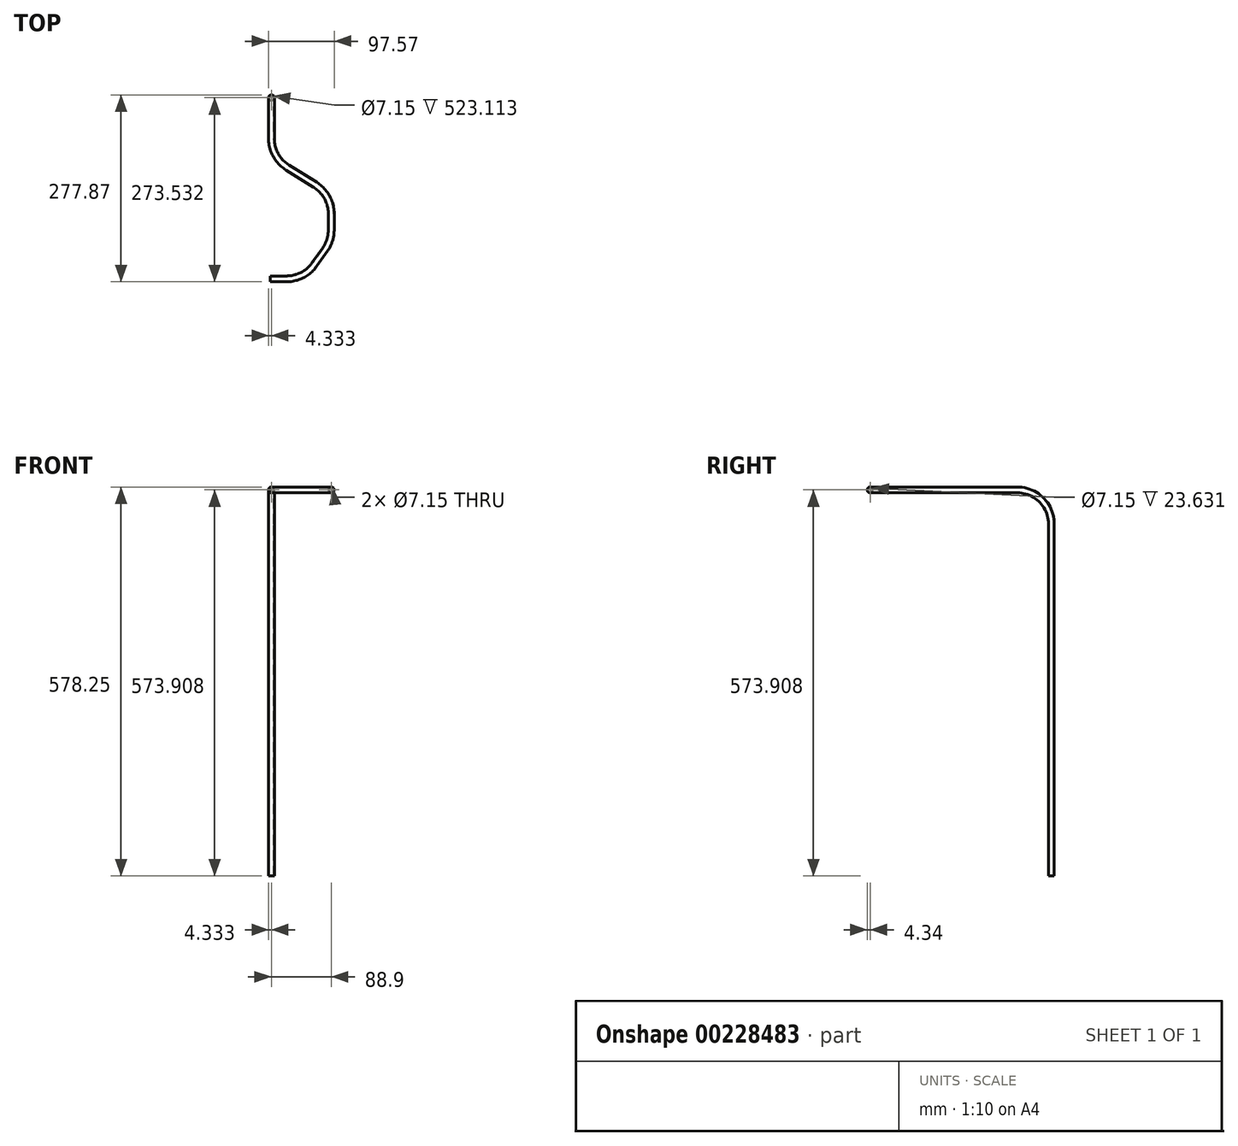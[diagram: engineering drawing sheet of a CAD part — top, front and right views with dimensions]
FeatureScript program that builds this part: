
annotation { "Feature Type Name" : "Feature", "Feature Type Description" : "" }
export const myFeature = defineFeature(function(context is Context, id is Id, definition is map)
    precondition{}
    {
        {
            var Q0;
            Q0=qCreatedBy(makeId("Top.planeOp"),FACE);
            var sketch = newSketch(context, id + "F0", { "sketchPlane" : qUnion([Q0])});
            skLineSegment(sketch, "E0", {"start": v(0, 0) * mm, "end": v(80.3, 0) * mm});
            skLineSegment(sketch, "E1", {"start": v(80.3, 0) * mm, "end": v(80.3, -94.46) * mm});
            skLineSegment(sketch, "E2", {"start": v(80.3, -94.46) * mm, "end": v(54.9, -94.46) * mm});
            skLineSegment(sketch, "E3", {"start": v(0, 0) * mm, "end": v(1.24, 0) * mm});
            skLineSegment(sketch, "E4", {"start": v(1.24, 0) * mm, "end": v(1.24, -0.8) * mm});
            skLineSegment(sketch, "E5", {"start": v(1.24, -0.8) * mm, "end": v(26.64, -0.8) * mm});
            skLineSegment(sketch, "E6", {"start": v(0, 0) * mm, "end": v(82.11, 0) * mm});
            skLineSegment(sketch, "E7.MirrorCS", {"start": v(82.11, 0) * mm, "end": v(82.11, 174.73) * mm});
            skLineSegment(sketch, "E8.MirrorCS", {"start": v(82.11, 174.73) * mm, "end": v(56.71, 174.73) * mm});
            skPoint(sketch, "E9.end.orphan", {"position": v(56.71, -174.73) * mm});
            skPoint(sketch, "E10.end.orphan", {"position": v(82.11, -174.73) * mm});
            skSolve(sketch);
        }
        {
            var Q0;
            Q0=sQuery(id+"F0.wireOp",EDGE,"E5");
            cPlane(context, id + "F1", {"entities" : qUnion([Q0]), "cplaneType" : CPlaneType.LINE_ANGLE, "offset" : 25.4 * mm, "angle" : 0 * degree, "width" : 152.4 * mm, "height" : 152.4 * mm});
        }
        {
            var Q0;
            Q0=qCreatedBy(id+"F1.planeOp",FACE);
            var sketch = newSketch(context, id + "F2", { "sketchPlane" : qUnion([Q0])});
            skLineSegment(sketch, "E11", {"start": v(-26.64, 0) * mm, "end": v(-26.64, 1312.2) * mm});
            skLineSegment(sketch, "E12", {"start": v(-26.64, 1312.2) * mm, "end": v(-1.24, 1312.2) * mm});
            skSolve(sketch);
        }
        {
            var Q0;
            Q0=sQuery(id+"F0.wireOp",EDGE,"E8.MirrorCS");
            cPlane(context, id + "F3", {"entities" : qUnion([Q0]), "cplaneType" : CPlaneType.LINE_ANGLE, "offset" : 25.4 * mm, "angle" : 0 * degree, "width" : 152.4 * mm, "height" : 152.4 * mm});
        }
        {
            var Q0;
            Q0=qCreatedBy(id+"F3.planeOp",FACE);
            var sketch = newSketch(context, id + "F4", { "sketchPlane" : qUnion([Q0])});
            skLineSegment(sketch, "E13", {"start": v(82.11, 0) * mm, "end": v(82.11, 801.7) * mm});
            skLineSegment(sketch, "E14", {"start": v(82.11, 801.7) * mm, "end": v(56.71, 801.7) * mm});
            skSolve(sketch);
        }
        {
            var Q0;
            Q0=sQuery(id+"F0.wireOp",EDGE,"E2");
            cPlane(context, id + "F5", {"entities" : qUnion([Q0]), "cplaneType" : CPlaneType.LINE_ANGLE, "offset" : 25.4 * mm, "angle" : 0 * degree, "width" : 152.4 * mm, "height" : 152.4 * mm});
        }
        {
            var Q0;
            Q0=qCreatedBy(id+"F5.planeOp",FACE);
            var sketch = newSketch(context, id + "F6", { "sketchPlane" : qUnion([Q0])});
            skLineSegment(sketch, "E15", {"start": v(80.3, 0) * mm, "end": v(80.3, 1375.6) * mm});
            skLineSegment(sketch, "E16", {"start": v(80.3, 1375.6) * mm, "end": v(54.9, 1375.6) * mm});
            skSolve(sketch);
        }
        {
            var Q0;
            Q0=sQuery(id+"F6.wireOp",EDGE,"E16");
            cPlane(context, id + "F7", {"entities" : qUnion([Q0]), "cplaneType" : CPlaneType.LINE_ANGLE, "offset" : 25.4 * mm, "angle" : 90 * degree, "width" : 152.4 * mm, "height" : 152.4 * mm});
        }
        {
            var Q0;
            Q0=qCreatedBy(id+"F7.planeOp",FACE);
            var sketch = newSketch(context, id + "F8", { "sketchPlane" : qUnion([Q0])});
            skLineSegment(sketch, "E17", {"start": v(80.3, -94.46) * mm, "end": v(80.3, -69.06) * mm});
            skSolve(sketch);
        }
        {
            var Q0;
            Q0=sQuery(id+"F8.wireOp",EDGE,"E17");
            cPlane(context, id + "F9", {"entities" : qUnion([Q0]), "cplaneType" : CPlaneType.LINE_ANGLE, "offset" : 25.4 * mm, "angle" : 90 * degree, "width" : 152.4 * mm, "height" : 152.4 * mm});
        }
        {
            var Q0;
            Q0=qCreatedBy(id+"F9.planeOp",FACE);
            var sketch = newSketch(context, id + "F10", { "sketchPlane" : qUnion([Q0])});
            skCircle(sketch, "E18", {"center": v(-94.46, 1375.6) * mm, "radius": 4.34 * mm});
            skSolve(sketch);
        }
        {
            var Q0;
            Q0=sQuery(id+"F2.wireOp",EDGE,"E12");
            cPlane(context, id + "F11", {"entities" : qUnion([Q0]), "cplaneType" : CPlaneType.LINE_ANGLE, "offset" : 25.4 * mm, "angle" : 90 * degree, "width" : 152.4 * mm, "height" : 152.4 * mm});
        }
        {
            var Q0;
            Q0=sQuery(id+"F4.wireOp",EDGE,"E14");
            cPlane(context, id + "F12", {"entities" : qUnion([Q0]), "cplaneType" : CPlaneType.LINE_ANGLE, "offset" : 25.4 * mm, "angle" : 90 * degree, "width" : 152.4 * mm, "height" : 152.4 * mm});
        }
        {
            var Q0;
            Q0=qCreatedBy(id+"F12.planeOp",FACE);
            var sketch = newSketch(context, id + "F13", { "sketchPlane" : qUnion([Q0])});
            skCircle(sketch, "E19", {"center": v(82.11, 174.73) * mm, "radius": 4.34 * mm});
            skSolve(sketch);
        }
        {
            var Q0;
            Q0=sQuery(id+"F4.wireOp",EDGE,"E14");
            cPlane(context, id + "F14", {"entities" : qUnion([Q0]), "cplaneType" : CPlaneType.LINE_ANGLE, "offset" : 25.4 * mm, "angle" : 0 * degree, "width" : 152.4 * mm, "height" : 152.4 * mm});
        }
        {
            var Q0;
            Q0=qCreatedBy(id+"F14.planeOp",FACE);
            var sketch = newSketch(context, id + "F15", { "sketchPlane" : qUnion([Q0])});
            skLineSegment(sketch, "E20", {"start": v(82.11, 801.7) * mm, "end": v(82.11, 877.9) * mm});
            skSolve(sketch);
        }
        {
            var Q0;
            Q0=qCreatedBy(id+"F7.planeOp",FACE);
            var sketch = newSketch(context, id + "F16", { "sketchPlane" : qUnion([Q0])});
            skLineSegment(sketch, "E21", {"start": v(80.3, -94.46) * mm, "end": v(104.69, -94.46) * mm});
            skLineSegment(sketch, "E22", {"start": v(146.27, -72.85) * mm, "end": v(161.8, -50.73) * mm});
            skLineSegment(sketch, "E23", {"start": v(171.01, -21.54) * mm, "end": v(171.01, 2.27) * mm});
            skLineSegment(sketch, "E24", {"start": v(147.06, 45.39) * mm, "end": v(106.06, 70.92) * mm});
            skLineSegment(sketch, "E25", {"start": v(82.11, 114.04) * mm, "end": v(82.11, 174.73) * mm});
            skLineSegment(sketch, "E26", {"start": v(171.01, 30.48) * mm, "end": v(82.11, 30.48) * mm});
            skPoint(sketch, "E27.visualSharp", {"position": v(131.1, -94.46) * mm});
            skArc(sketch, "E27.filletArc", {"start": v(104.69, -94.46) * mm, "mid": v(128.12, -88.73) * mm, "end": v(146.27, -72.85) * mm});
            skPoint(sketch, "E28.visualSharp", {"position": v(171.01, -37.6) * mm});
            skArc(sketch, "E28.filletArc", {"start": v(161.8, -50.73) * mm, "mid": v(168.65, -36.85) * mm, "end": v(171.01, -21.54) * mm});
            skPoint(sketch, "E29.visualSharp", {"position": v(171.01, 30.48) * mm});
            skArc(sketch, "E29.filletArc", {"start": v(171.01, 2.27) * mm, "mid": v(164.62, 26.93) * mm, "end": v(147.06, 45.39) * mm});
            skPoint(sketch, "E30.visualSharp", {"position": v(82.11, 85.83) * mm});
            skArc(sketch, "E30.filletArc", {"start": v(82.11, 114.04) * mm, "mid": v(88.5, 89.38) * mm, "end": v(106.06, 70.92) * mm});
            skSolve(sketch);
        }
        {
            var Q0;
            Q0=sQuery(id+"F15.wireOp",VERTEX,"E20.start");
            var Q1;
            Q1=sQuery(id+"F15.wireOp",VERTEX,"E20.end");
            var Q2;
            Q2=sQuery(id+"F16.wireOp",VERTEX,"E30.filletArc.start");
            cPlane(context, id + "F17", {"entities" : qUnion([Q0, Q1, Q2]), "cplaneType" : CPlaneType.THREE_POINT, "offset" : 25.4 * mm, "width" : 152.4 * mm, "height" : 152.4 * mm});
        }
        {
            var Q0;
            Q0=qCreatedBy(id+"F17.planeOp",FACE);
            var sketch = newSketch(context, id + "F18", { "sketchPlane" : qUnion([Q0])});
            skLineSegment(sketch, "E31", {"start": v(-114.04, 1375.6) * mm, "end": v(-123.93, 1375.6) * mm});
            skLineSegment(sketch, "E32", {"start": v(-174.73, 1324.8) * mm, "end": v(-174.73, 877.9) * mm});
            skPoint(sketch, "E33.visualSharp", {"position": v(-174.73, 1375.6) * mm});
            skArc(sketch, "E33.filletArc", {"start": v(-123.93, 1375.6) * mm, "mid": v(-159.85, 1360.73) * mm, "end": v(-174.73, 1324.8) * mm});
            skSolve(sketch);
        }
        {
            var Q0;
            Q0=makeQuery(id+"F13.imprint","IMPRINT",FACE,{"disambiguationData":[TD([[makeQuery(id+"F13.imprint","IMPRINT",EDGE,{"derivedFrom":sQuery(id+"F13.wireOp",EDGE,"E19")}),1.0]])]});
            var Q1;
            Q1=sQuery(id+"F15.wireOp",EDGE,"E20");
            var Q2;
            Q2=sQuery(id+"F18.wireOp",EDGE,"E32");
            var Q3;
            Q3=sQuery(id+"F18.wireOp",EDGE,"E33.filletArc");
            var Q4;
            Q4=sQuery(id+"F18.wireOp",EDGE,"E31");
            var Q5;
            Q5=sQuery(id+"F16.wireOp",EDGE,"E30.filletArc");
            var Q6;
            Q6=sQuery(id+"F16.wireOp",EDGE,"E24");
            var Q7;
            Q7=sQuery(id+"F16.wireOp",EDGE,"E29.filletArc");
            var Q8;
            Q8=sQuery(id+"F16.wireOp",EDGE,"E23");
            var Q9;
            Q9=sQuery(id+"F16.wireOp",EDGE,"E28.filletArc");
            var Q10;
            Q10=sQuery(id+"F16.wireOp",EDGE,"E22");
            var Q11;
            Q11=sQuery(id+"F16.wireOp",EDGE,"E27.filletArc");
            var Q12;
            Q12=sQuery(id+"F16.wireOp",EDGE,"E21");
            sweep(context, id + "F19", {"profiles" : qUnion([Q0]), "path" : qUnion([Q1, Q2, Q3, Q4, Q5, Q6, Q7, Q8, Q9, Q10, Q11, Q12])});
        }
        {
            var Q0;
            Q0=makeQuery(id+"F19.opSweep","CAP_FACE",FACE,{"disambiguationData":[OSD([sQuery(id+"F13.wireOp",EDGE,"E19"),sQuery(id+"F15.wireOp",VERTEX,"E20.start")])],"isStart":true});
            shell(context, id + "F20", {"entities" : qUnion([Q0]), "thickness" : 0.76 * mm});
        }
    });
